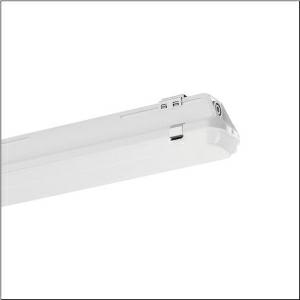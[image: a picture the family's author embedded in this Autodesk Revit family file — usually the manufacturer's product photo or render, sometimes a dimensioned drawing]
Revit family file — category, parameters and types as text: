
# Revit family: monsun_21_51fb10mp480c
name_source: partatom
category: Lighting Fixtures
units: mm (PartAtom-declared; Revit-internal decimal feet)

## family parameters
Cut with Voids When Loaded = No
Host = Face
Light Source = No
Part Type = Normal
Room Calculation Point = No
Round Connector Dimension = Use Diameter
Shared = No

## types (1)
- --- (1 x LED, 8550 lm, 45.6 W, 4000K)
    Apparent Load = 46 VA
    CIE Flux Codes = 47 77 93 94 100
    Color Rendering = 80
    Color Temperature = 4000K
    Default Elevation = 1800 mm
    Description = Monsun 21, damp-proof luminaire, chain hanger, primary optical cover: enclosure, of PMMA, light emission: direct distribution, primary light characteristic: symmetric, installation type: suspended mounting, surface-mounted, horizontal mounting, vertical mounting, LED, rated luminous flux: 8.550lm, luminous efficacy: 188lm/W, light colour: 840, colour temperature: 4000K, control gear: ON/OFF Multilumen, with terminal, 3-pole, max. 2.5mm², mains connection: 220..240V, AC, 50/60Hz, rated input power: 46W, housing, of glass-fibre reinforced polyester, uncoated, bright grey, incl. chain hanger, length: 1.590mm, width: 90mm, height: 88mm, clip for enclosure, of stainless steel (V2A), ceiling mounting element, of stainless steel (V2A), chain hanger, of stainless steel (V2A), protection rating (complete): IP66, insulation class (complete): insulation class I (protective earthing), certification: CE, ENEC, VDE, UKCA, protection symbol: D, impact resistance: IK04, permissible operating ambient temperature: -25..+35°C, standard: EN 50419, EN 60598-2-1, corresponds to IFS (International Featured Standards) requirements for safety and quality in the food industry, for indoor or canopied outdoor use, no direct snow, no direct sun, no direct rain, LABS conformity tested according to VDMA 24364:2018-05, contact your sales advisor before using the luminaires in applications with unclear chemical exposure, large temperature fluctuations or condensation-forming humidity, packaging unit: 1 piece
    Height = 89 mm
    Lamp = 1 x LED
    Lamp Light Flux = 8550 lm
    Lamp Power = 45.6 W
    Lamp count = 1
    Length = 1590 mm
    Luminous efficacy = 188 lm/W
    Manufacturer = Siteco
    ModVariant = No
    Model = 51FB10MP480C
    Mounting Place = Ceiling
    Mounting Type = Surface mounted
    Number of Poles = 1
    OnlyDefault = Yes
    Power Factor = 1
    Product Name = Monsun 21
    Product group = damp-proof luminaire
    ProductGroupID = 300
    Protection Class = Protection class I
    Protection Degree = IP 66
    RLX_Detail_Level = 1
    RLX_Emergency_Light_Flux = 0 lm
    RLX_Emergency_Type = 0
    RLX_Emergency_Type_DB = No
    RlxData = <blob elided: 89889 chars, md5=fef58a27>
    Socket = socket
    Standby Power = 0 W
    System Light Flux = 8550 lm
    System Power = 46 W
    Type Comments = factory setting: luminous flux: 100 % | (A | C | E) | 106 mA
    Type Image = l_1319656.jpg
    URL = http://relux.com
    VarID = @adj_038397
    Voltage = 0 V
    Weight = 0.00 kg
    Width = 90 mm

## geometry (parser evidence)
native form markers: Blend x4, Sweep x14
no freeform markers — native parametric forms only
